# Revit family: Basin-Vanity_Sink-American_Standard-Studio_S-1296000
name_source: partatom
category: Plumbing Fixtures
units: mm (PartAtom-declared; Revit-internal decimal feet)

## family parameters
Always vertical = No
Cut with Voids When Loaded = Yes
OmniClass Number = 23.45.05.14.14
OmniClass Title = Sinks/Lavatories
Part Type = Normal
Room Calculation Point = No
Round Connector Dimension = Use Diameter
Shared = Yes
Work Plane-Based = Yes

## types (1)
- 1296000.020
    7720018 Optional decorative p-trap drain = No
    7813001 Above Counter Sink top with CHO hole = No
    87222000 Vanity leg set = No
    8726033 33" Double Drawer Vanity = No
    8727000 Vanity Middle = No
    ADA Compliant = Yes
    ASME A112.18.1/CSA B125.1 = Yes
    Assembly Code = D2010310
    Basin Shape = Oval
    CW Connection = Yes
    CWFU = 1.5
    Connection Size = 1/2"
    Default Elevation = 31"
    Description = Studio® S Above Counter Sink and Optional Furniture VITREOUS CHINA  BARRIER FREE
    Faucet to Sink = 2"
    Faucet to Sink Constraint = 0"
    Finish = Vitreous China-American Standard-020-White
    Finished Wall to Faucet = 1 1/2"
    Finished Wall to Faucet Constraint = 0"
    HW Connection = Yes
    HWFU = 1.5
    Height = 1 7/8"
    Installation Type = Counter
    Length = 14"
    Manufacturer = American Standard
    Material = Vitreous China-American Standard-020-White
    Model = 1296000.020
    Price = Prices may vary. Please consult Manufacturer Representative for most up-to-date price list.
    Product Documentation Link = https://americanstandard.box.com
    Product Page URL = https://www.americanstandard-us.com
    Revised Date = 10/18/2021
    Sink To Front Edge = 3"
    Sink to Front Edge Constraint = 0"
    Type Comments = ADA Not compliant when used with optional furniture.
    URL = http://www.americanstandard-us.com
    Vent Connection = No
    WFU = 2
    Warranty Documentation Link = https://www.americanstandard-us.com
    Waste Connection = Yes
    Waste Connection Diameter = 1 1/4"
    Width = 22 1/2"

## geometry (parser evidence)
native form markers: Sweep x2
no freeform markers — native parametric forms only
